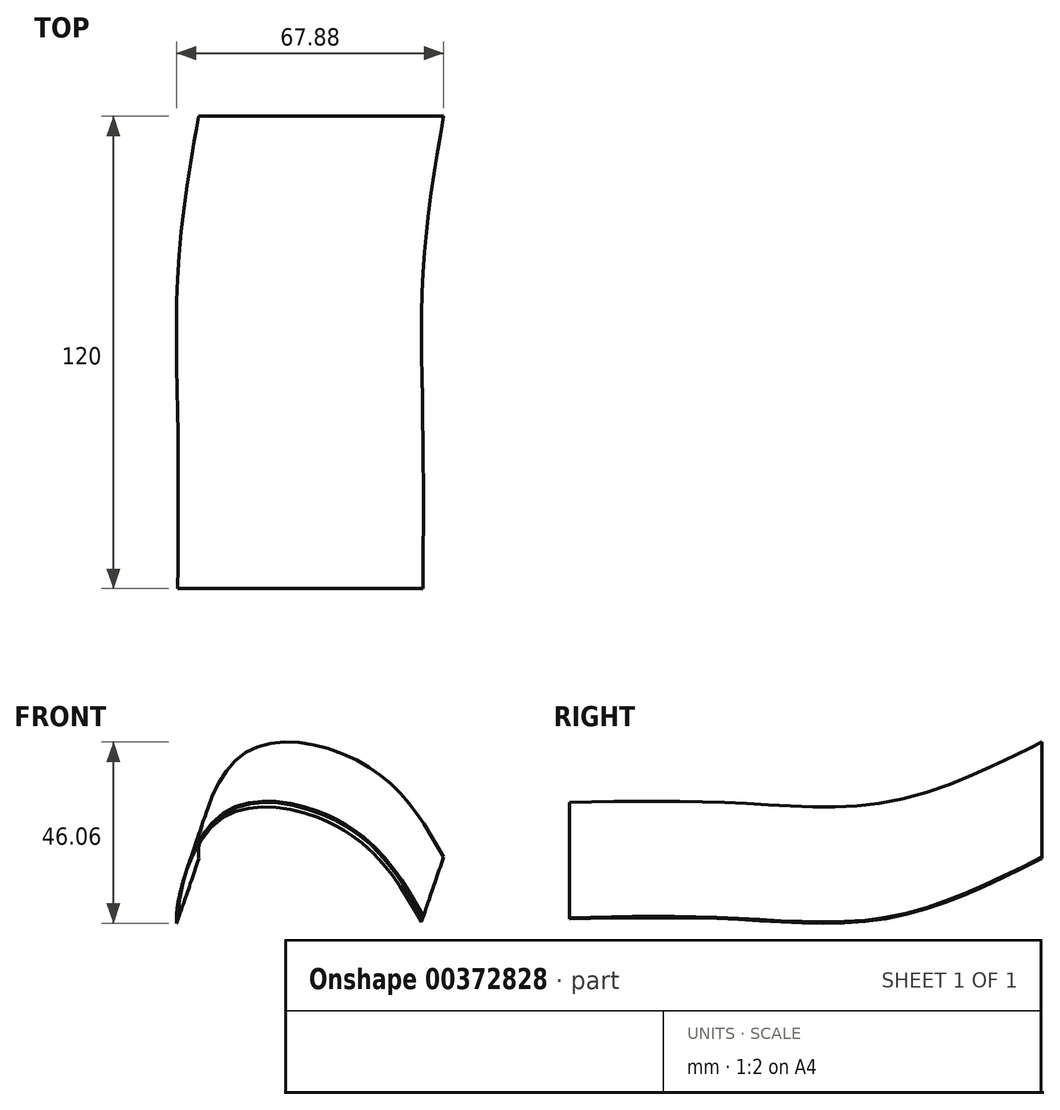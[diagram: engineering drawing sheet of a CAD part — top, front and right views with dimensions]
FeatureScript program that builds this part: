
annotation { "Feature Type Name" : "Feature", "Feature Type Description" : "" }
export const myFeature = defineFeature(function(context is Context, id is Id, definition is map)
    precondition{}
    {
        {
            var Q0;
            Q0=qCreatedBy(makeId("Front.planeOp"),FACE);
            cPlane(context, id + "F0", {"entities" : qUnion([Q0]), "cplaneType" : CPlaneType.OFFSET, "offset" : 40 * mm, "width" : 150 * mm, "height" : 150 * mm});
        }
        {
            var Q0;
            Q0=qCreatedBy(id+"F0.planeOp",FACE);
            cPlane(context, id + "F1", {"entities" : qUnion([Q0]), "cplaneType" : CPlaneType.OFFSET, "offset" : 40 * mm, "width" : 150 * mm, "height" : 150 * mm});
        }
        {
            var Q0;
            Q0=qCreatedBy(id+"F1.planeOp",FACE);
            cPlane(context, id + "F2", {"entities" : qUnion([Q0]), "cplaneType" : CPlaneType.OFFSET, "offset" : 40 * mm, "width" : 150 * mm, "height" : 150 * mm});
        }
        {
            var Q0;
            Q0=qCreatedBy(makeId("Front.planeOp"),FACE);
            var sketch = newSketch(context, id + "F3", { "sketchPlane" : qUnion([Q0])});
            skFitSpline(sketch, "E0", {"points": [v(39.12, -2.85) * mm, v(20.46, 19.83) * mm, v(-12.08, 23.12) * mm, v(-23.02, 0) * mm, v(-23.04, -3.19) * mm], "startDerivative": vector(-47.53, 83.81) * mm, "endDerivative": vector(2.65, -22.13) * mm});
            skSolve(sketch);
        }
        {
            var Q0;
            Q0=qCreatedBy(id+"F0.planeOp",FACE);
            var sketch = newSketch(context, id + "F4", { "sketchPlane" : qUnion([Q0])});
            skFitSpline(sketch, "E1", {"points": [v(33.87, -18.23) * mm, v(15.21, 4.44) * mm, v(-17.33, 7.74) * mm, v(-28.26, -15.38) * mm, v(-28.29, -18.57) * mm], "startDerivative": vector(-47.53, 83.81) * mm, "endDerivative": vector(2.65, -22.13) * mm});
            skSolve(sketch);
        }
        {
            var Q0;
            Q0=qCreatedBy(id+"F1.planeOp",FACE);
            var sketch = newSketch(context, id + "F5", { "sketchPlane" : qUnion([Q0])});
            skFitSpline(sketch, "E2", {"points": [v(33.87, -18.23) * mm, v(15.21, 4.44) * mm, v(-17.33, 7.74) * mm, v(-28.26, -15.38) * mm, v(-28.29, -18.57) * mm], "startDerivative": vector(-47.53, 83.81) * mm, "endDerivative": vector(2.65, -22.13) * mm});
            skSolve(sketch);
        }
        {
            var Q0;
            Q0=qCreatedBy(id+"F2.planeOp",FACE);
            var sketch = newSketch(context, id + "F6", { "sketchPlane" : qUnion([Q0])});
            skFitSpline(sketch, "E3", {"points": [v(33.87, -18.23) * mm, v(15.21, 4.44) * mm, v(-17.33, 7.74) * mm, v(-28.26, -15.38) * mm, v(-28.29, -18.57) * mm], "startDerivative": vector(-47.53, 83.81) * mm, "endDerivative": vector(2.65, -22.13) * mm});
            skSolve(sketch);
        }
        {
            var Q0;
            Q0=sQuery(id+"F3.wireOp",EDGE,"E0");
            var Q1;
            Q1=sQuery(id+"F4.wireOp",EDGE,"E1");
            var Q2;
            Q2=sQuery(id+"F5.wireOp",EDGE,"E2");
            var Q3;
            Q3=sQuery(id+"F6.wireOp",EDGE,"E3");
            loft(context, id + "F7", {"bodyType" : ToolBodyType.SURFACE, "operationType" : NewBodyOperationType.INTERSECT, "wireProfilesArray" : [{ "wireProfileEntities" : qUnion([Q0]) }, { "wireProfileEntities" : qUnion([Q1]) }, { "wireProfileEntities" : qUnion([Q2]) }, { "wireProfileEntities" : qUnion([Q3]) }]});
        }
    });
